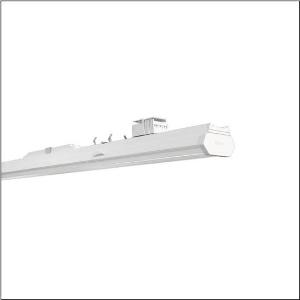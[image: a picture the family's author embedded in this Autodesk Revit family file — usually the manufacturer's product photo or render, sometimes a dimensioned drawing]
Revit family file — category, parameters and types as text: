
# Revit family: licross_21_protected_mo_52tp127n485g
name_source: partatom
category: Lighting Fixtures
units: mm (PartAtom-declared; Revit-internal decimal feet)

## family parameters
Cut with Voids When Loaded = No
Host = Face
Light Source = No
Part Type = Normal
Room Calculation Point = No
Round Connector Dimension = Use Diameter
Shared = No

## types (1)
- Licross 21 Protected MO (1 x LED, 8610 lm, 47.9 W, 4000K)
    Apparent Load = 48 VA
    CIE Flux Codes = 73 92 98 99 100
    Color Rendering = 80
    Color Temperature = 4000K
    Default Elevation = 1800 mm
    Description = Licross 21 Protected MO, luminaire insert, of sheet steel, galvanised, coil coated, white, length: 1.500mm, width: 90mm, height: 101mm, LED rated luminous flux: 8.610lm, light colour: 840, SDCM (Standard Deviation of Colour Matching)MacAdam ≤ 3 SDCM (initial), control gear: ON/OFF, with plug, 3-pole, with phase selection, mains connection: 220..240V, AC, 50/60Hz, rated input power: 48W, internal wiring halogen-free, primary light control with lens, of plastic, primary optical cover: cover, of PMMA, light emission: direct distribution, primary light characteristic: symmetric, protection rating (complete): IP64, insulation class (complete): insulation class I (protective earthing), certification: CE, ENEC, VDE, UKCA, protection symbol: D if used in an environment with conductive dust loads with corresponding accessories, impact resistance: IK06, permissible ambient temperature for indoor applications: -35..+45°C, corresponds to IFS (International Featured Standards) requirements for safety and quality in the food industry, reducing of maximum allowable ambient temperature of 5°C with ceiling mounting, LABS conformity tested according to VDMA 24364:2018-05, The light source and the operating device comply with the requirements of the Ecodesign Regulation (EU) 2019/2020 and are replaceable in accordance with this regulation, packaging unit: 1 piece
    Height = 92 mm
    Lamp = 1 x LED
    Lamp Light Flux = 8610 lm
    Lamp Power = 47.9 W
    Lamp count = 1
    Length = 1500 mm
    Luminous efficacy = 180 lm/W
    Manufacturer = Siteco
    ModVariant = No
    Model = 52TP127N485G
    Mounting Place = Ceiling
    Mounting Type = Pendant
    Number of Poles = 1
    OnlyDefault = Yes
    Power Factor = 1
    Product Name = Licross 21 Protected MO
    Product group = luminaire insert | ceiling pendant
    ProductGroupID = 901
    Protection Class = Protection class I
    Protection Degree = IP 64
    RLX_Detail_Level = 1
    RLX_Emergency_Light_Flux = 0 lm
    RLX_Emergency_Type = 0
    RLX_Emergency_Type_DB = No
    RlxData = <blob elided: 21025 chars, md5=214f43b2>
    Socket = socket
    Standby Power = 0 W
    System Light Flux = 8610 lm
    System Power = 48 W
    Type Comments = Product without accessories
    Type Image = l_1256148.jpg
    URL = http://relux.com
    VarID = ---
    Voltage = 0 V
    Weight = 0.00 kg
    Width = 88 mm

## geometry (parser evidence)
native form markers: Blend x4, Sweep x11
no freeform markers — native parametric forms only
